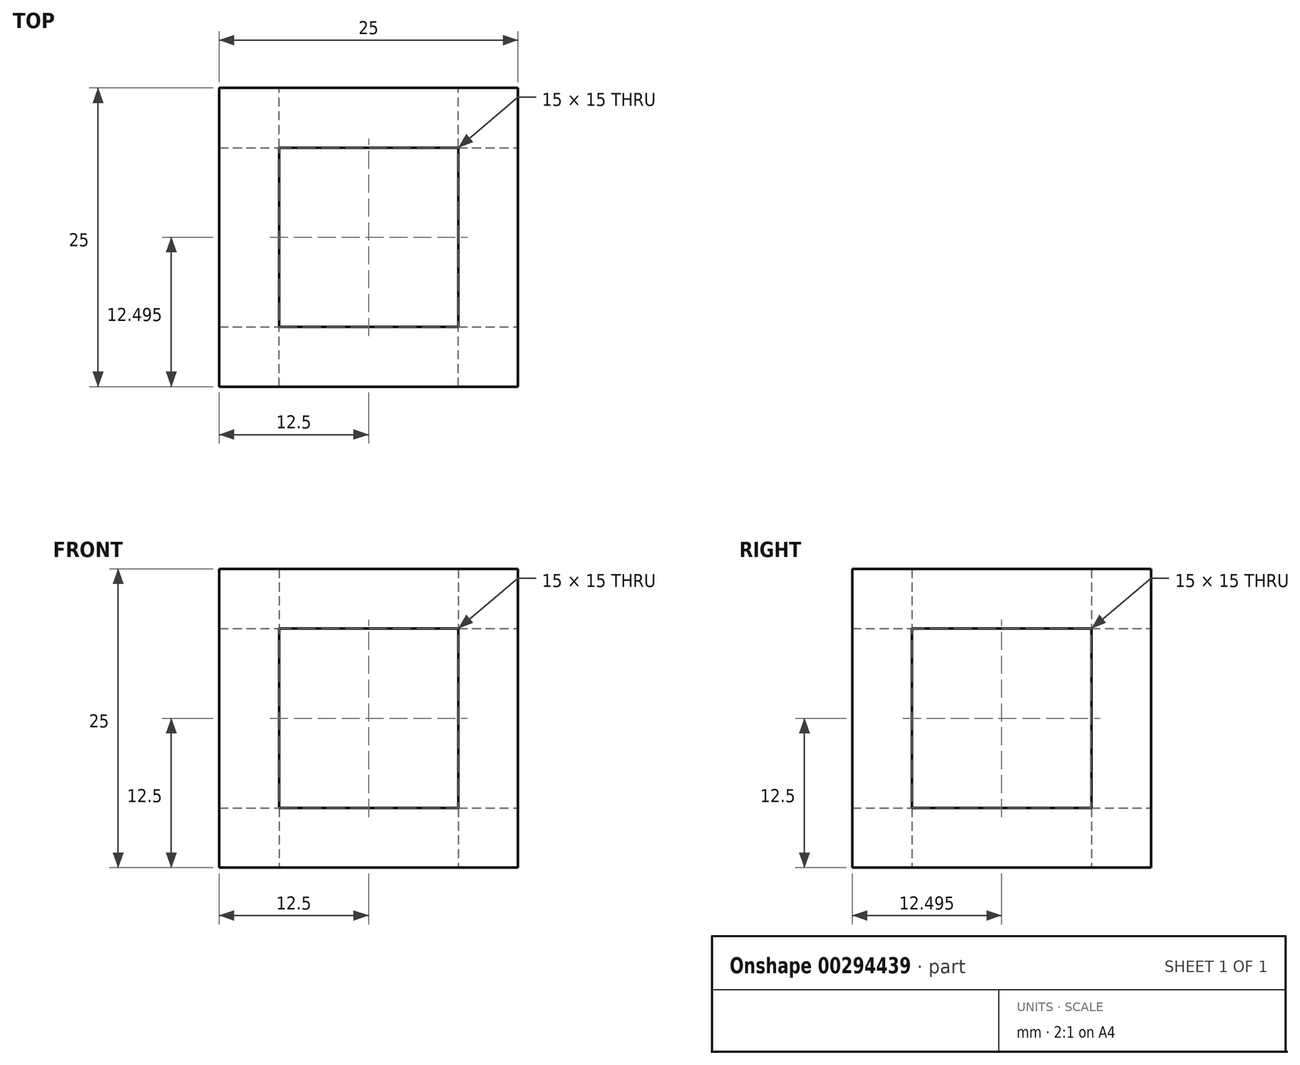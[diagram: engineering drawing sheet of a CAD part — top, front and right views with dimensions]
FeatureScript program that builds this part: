
annotation { "Feature Type Name" : "Feature", "Feature Type Description" : "" }
export const myFeature = defineFeature(function(context is Context, id is Id, definition is map)
    precondition{}
    {
        {
            var Q0;
            Q0=qCreatedBy(makeId("Top.planeOp"),FACE);
            var sketch = newSketch(context, id + "F0", { "sketchPlane" : qUnion([Q0])});
            skLineSegment(sketch, "E0.bottom", {"start": v(-3.59, 0.07) * mm, "end": v(21.41, 0.07) * mm});
            skLineSegment(sketch, "E0.top", {"start": v(-3.59, -24.93) * mm, "end": v(21.41, -24.93) * mm});
            skLineSegment(sketch, "E0.left", {"start": v(-3.59, 0.07) * mm, "end": v(-3.59, -24.93) * mm});
            skLineSegment(sketch, "E0.right", {"start": v(21.41, 0.07) * mm, "end": v(21.41, -24.93) * mm});
            skLineSegment(sketch, "E1.bottom", {"start": v(16.41, -19.93) * mm, "end": v(1.41, -19.93) * mm});
            skLineSegment(sketch, "E1.top", {"start": v(16.41, -4.93) * mm, "end": v(1.41, -4.93) * mm});
            skLineSegment(sketch, "E1.left", {"start": v(16.41, -19.93) * mm, "end": v(16.41, -4.93) * mm});
            skLineSegment(sketch, "E1.right", {"start": v(1.41, -19.93) * mm, "end": v(1.41, -4.93) * mm});
            skPoint(sketch, "E1.middle", {"position": v(8.91, -12.43) * mm});
            skPoint(sketch, "E1.middle.positionSnap0", {"position": v(21.41, -12.43) * mm});
            skPoint(sketch, "E1.middle.positionSnap1", {"position": v(8.91, -24.93) * mm});
            skPoint(sketch, "E1.centerSnap0", {"position": v(21.41, -12.43) * mm});
            skPoint(sketch, "E1.centerSnap1", {"position": v(8.91, -24.93) * mm});
            skSolve(sketch);
        }
        {
            var Q0;
            Q0 = qSketchRegion(id + "F0", true);
            extrude(context, id + "F1", {"entities" : qUnion([Q0]), "depth" : 25 * mm});
        }
        {
            var Q0;
            Q0=makeQuery(id+"F1.opExtrude","SWEPT_FACE",FACE,{"disambiguationData":[OSD([sQuery(id+"F0.wireOp",EDGE,"E0.right")])]});
            var sketch = newSketch(context, id + "F2", { "sketchPlane" : qUnion([Q0])});
            skLineSegment(sketch, "E2.bottom", {"start": v(-19.93, 5) * mm, "end": v(-4.93, 5) * mm});
            skLineSegment(sketch, "E2.top", {"start": v(-19.93, 20) * mm, "end": v(-4.93, 20) * mm});
            skLineSegment(sketch, "E2.left", {"start": v(-19.93, 5) * mm, "end": v(-19.93, 20) * mm});
            skLineSegment(sketch, "E2.right", {"start": v(-4.93, 5) * mm, "end": v(-4.93, 20) * mm});
            skPoint(sketch, "E2.middle", {"position": v(-12.43, 12.5) * mm});
            skPoint(sketch, "E2.middle.positionSnap0", {"position": v(-24.93, 12.5) * mm});
            skPoint(sketch, "E2.middle.positionSnap1", {"position": v(-12.43, 25) * mm});
            skPoint(sketch, "E2.centerSnap0", {"position": v(-24.93, 12.5) * mm});
            skPoint(sketch, "E2.centerSnap1", {"position": v(-12.43, 25) * mm});
            skSolve(sketch);
        }
        {
            var Q0;
            Q0=makeQuery(id+"F2.imprint","IMPRINT",FACE,{"disambiguationData":[TD([[makeQuery(id+"F2.imprint","IMPRINT",EDGE,{"derivedFrom":sQuery(id+"F2.wireOp",EDGE,"E2.bottom")}),1.0]])]});
            extrude(context, id + "F3", {"entities" : qUnion([Q0]), "operationType" : NewBodyOperationType.REMOVE, "oppositeDirection" : true, "depth" : 25 * mm});
        }
        {
            var Q0;
            Q0=makeQuery(id+"F1.opExtrude","SWEPT_FACE",FACE,{"disambiguationData":[OSD([sQuery(id+"F0.wireOp",EDGE,"E0.bottom")])]});
            var sketch = newSketch(context, id + "F4", { "sketchPlane" : qUnion([Q0])});
            skLineSegment(sketch, "E3.bottom", {"start": v(-1.41, 5) * mm, "end": v(-16.41, 5) * mm});
            skLineSegment(sketch, "E3.top", {"start": v(-1.41, 20) * mm, "end": v(-16.41, 20) * mm});
            skLineSegment(sketch, "E3.left", {"start": v(-1.41, 5) * mm, "end": v(-1.41, 20) * mm});
            skLineSegment(sketch, "E3.right", {"start": v(-16.41, 5) * mm, "end": v(-16.41, 20) * mm});
            skPoint(sketch, "E3.middle", {"position": v(-8.91, 12.5) * mm});
            skPoint(sketch, "E3.middle.positionSnap0", {"position": v(3.59, 12.5) * mm});
            skPoint(sketch, "E3.middle.positionSnap1", {"position": v(-8.91, 25) * mm});
            skPoint(sketch, "E3.centerSnap0", {"position": v(3.59, 12.5) * mm});
            skPoint(sketch, "E3.centerSnap1", {"position": v(-8.91, 25) * mm});
            skSolve(sketch);
        }
        {
            var Q0;
            Q0=makeQuery(id+"F4.imprint","IMPRINT",FACE,{"disambiguationData":[TD([[makeQuery(id+"F4.imprint","IMPRINT",EDGE,{"derivedFrom":sQuery(id+"F4.wireOp",EDGE,"E3.bottom")}),-1.0]])]});
            extrude(context, id + "F5", {"entities" : qUnion([Q0]), "operationType" : NewBodyOperationType.REMOVE, "oppositeDirection" : true, "depth" : 25 * mm});
        }
    });
